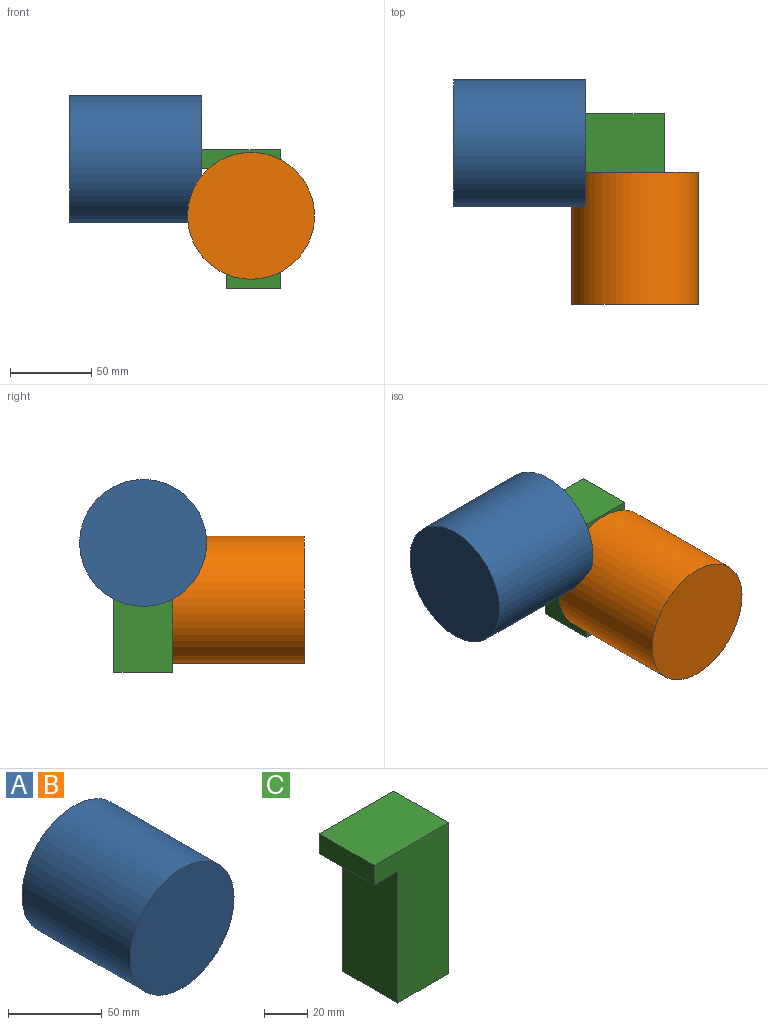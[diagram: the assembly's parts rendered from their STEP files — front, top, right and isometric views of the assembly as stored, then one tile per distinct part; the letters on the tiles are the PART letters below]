
ASSEMBLY  parts=3 mates=2
PART A: 3 faces, bbox 78.2x81.4x78.2 mm
  f0: cylinder r=39.12mm len=81.39mm, axis (0,1,0), area 20006mm2, adj f1,f2
  f1: plane 78.24x78.24mm, normal (0,-1,0), area 4807.7mm2, adj f0
  f2: plane 78.24x78.24mm, normal (0,1,0), area 4807.7mm2, adj f0
PART B: same geometry as A
PART C: 8 faces, bbox 48.5x35.9x85.4 mm
  f0: plane 48.53x35.9mm, normal (0,0,1), area 1742mm2, adj f1,f5,f6,f7
  f1: plane 35.9x11.15mm, normal (-1,0,0), area 400.1mm2, adj f0,f2,f6,f7
  f2: plane 35.9x15.23mm, normal (0,0,-1), area 546.7mm2, adj f1,f3,f6,f7
  f3: plane 74.25x35.9mm, normal (-1,0,0), area 2665.3mm2, adj f2,f4,f6,f7
  f4: plane 35.9x33.3mm, normal (0,0,-1), area 1195.3mm2, adj f3,f5,f6,f7
  f5: plane 85.39x35.9mm, normal (1,0,0), area 3065.5mm2, adj f0,f4,f6,f7
  f6: plane 85.39x48.53mm, normal (0,-1,0), area 3013.1mm2, adj f0,f1,f2,f3,f4,f5
  f7: plane 85.39x48.53mm, normal (0,1,0), area 3013.1mm2, adj f0,f1,f2,f3,f4,f5
PLACE A rot(axis=(-0.58,-0.58,-0.58),120deg) t=(25.39,-29.85,29.87)mm
PLACE B t=(55.9,-35.9,-17.07)mm
PLACE C at identity
MATE fastened A.f0 <-> C.f1  axis (1,0,0) through (25.39,-17.95,29.87)mm
MATE fastened B.f0 <-> C.f6  axis (0,1,0) through (55.9,-35.9,-5.16)mm
